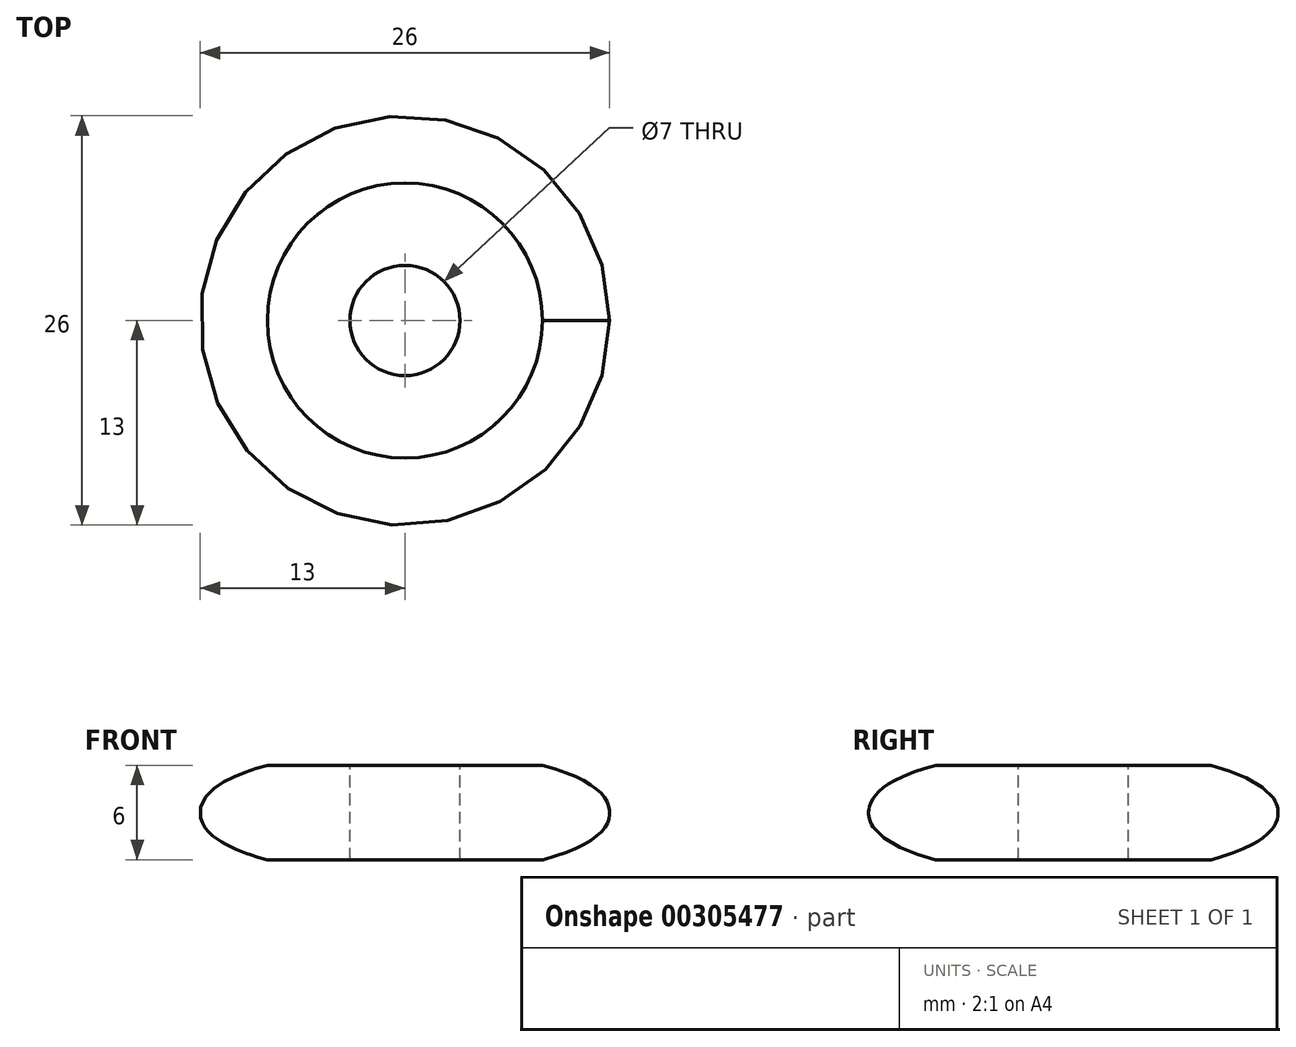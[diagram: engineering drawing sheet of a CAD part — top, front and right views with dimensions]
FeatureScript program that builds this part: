
annotation { "Feature Type Name" : "Feature", "Feature Type Description" : "" }
export const myFeature = defineFeature(function(context is Context, id is Id, definition is map)
    precondition{}
    {
        {
            var Q0;
            Q0=qCreatedBy(makeId("Front.planeOp"),FACE);
            var sketch = newSketch(context, id + "F0", { "sketchPlane" : qUnion([Q0])});
            skLineSegment(sketch, "E0", {"start": v(3.5, 4) * mm, "end": v(3.5, -4) * mm});
            skFitSpline(sketch, "E1", {"points": [v(3.5, 4) * mm, v(13, 0) * mm, v(3.5, -4) * mm], "startDerivative": vector(44.41, -6) * mm, "endDerivative": vector(-44.8, -6) * mm});
            skLineSegment(sketch, "E2", {"start": v(0, 2.85) * mm, "end": v(0, -3.78) * mm, "construction": true});
            skLineSegment(sketch, "E3", {"start": v(0, 0) * mm, "end": v(9.37, 0) * mm, "construction": true});
            skLineSegment(sketch, "E4.bottom", {"start": v(29.98, 3) * mm, "end": v(-29.98, 3) * mm});
            skLineSegment(sketch, "E4.top", {"start": v(29.98, -3) * mm, "end": v(-29.98, -3) * mm});
            skLineSegment(sketch, "E4.left", {"start": v(29.98, 3) * mm, "end": v(29.98, -3) * mm});
            skLineSegment(sketch, "E4.right", {"start": v(-29.98, 3) * mm, "end": v(-29.98, -3) * mm});
            skPoint(sketch, "E4.middle", {"position": v(0, 0) * mm});
            skSolve(sketch);
        }
        {
            var Q0;
            {var subQ0=sQuery(id+"F0.wireOp",EDGE,"E4.bottom");var subQ1=sQuery(id+"F0.wireOp",EDGE,"E0");var subQ2=makeQuery(id+"F0.imprint","INTERSECT",VERTEX,{"derivedFrom":[subQ1,subQ0]});Q0=makeQuery(id+"F0.imprint","IMPRINT",FACE,{"disambiguationData":[TD([[makeQuery(id+"F0.imprint","IMPRINT",EDGE,{"disambiguationData":[TD([[subQ2,-1.0]])],"derivedFrom":subQ1}),1.0]])]});}
            var Q1;
            Q1=sQuery(id+"F0.wireOp",EDGE,"E2");
            revolve(context, id + "F1", {"entities" : qUnion([Q0]), "axis" : qUnion([Q1]), "revolveType" : RevolveType.FULL});
        }
    });
